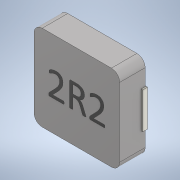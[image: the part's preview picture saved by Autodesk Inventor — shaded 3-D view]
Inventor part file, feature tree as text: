
AUTODESK INVENTOR PART (.ipt)
format: ipt  version: 2020.3 (Build 243373000, 373)  size: 268,800 bytes
history: native  units: mm
features: extrude x3, sketch x3, fillet x1
ambient origin geometry x8: Origin, YZ Plane, XZ Plane, XY Plane, X Axis, Y Axis, Z Axis, Center Point
bodies: Solid1 (feature_tree)
feature tree (7):
  extrude  "Extrusion1"  Depth=5.2mm
  extrude  "Extrusion2"  Depth=1.2mm
  fillet  "Fillet1"  Radius=0.1mm
  extrude  "Extrusion4"  Depth=5.4mm
  sketch  "Sketch1"  dims[d0=5.2mm d1=5.2mm]
  sketch  "Sketch2"  dims[d2=1.55mm d3=0.0mm d4=1.2mm d5=0.1mm]
  sketch  "Sketch3"  dims[d6=2.2mm d7=5.4mm d8=0.05mm d9=0.0mm d10=0.25mm d11=0.0mm d12=0.5mm d13=5.0mm d14=2.5mm d17=0.01mm d18=0.0mm]
